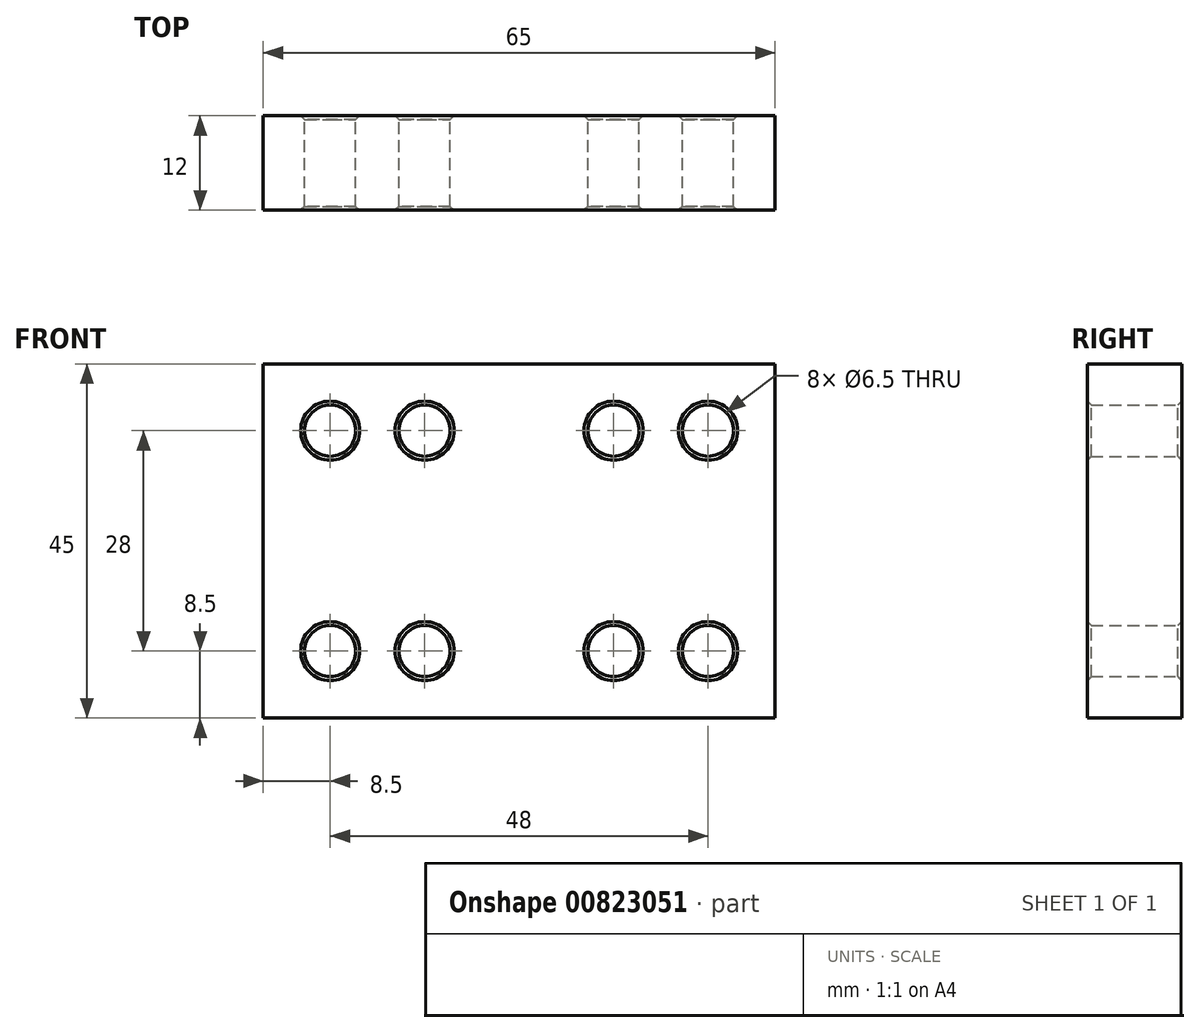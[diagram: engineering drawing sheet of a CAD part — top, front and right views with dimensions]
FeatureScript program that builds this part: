
annotation { "Feature Type Name" : "Feature", "Feature Type Description" : "" }
export const myFeature = defineFeature(function(context is Context, id is Id, definition is map)
    precondition{}
    {
        {
            var Q0;
            Q0=qCreatedBy(makeId("Front.planeOp"),FACE);
            var sketch = newSketch(context, id + "F0", { "sketchPlane" : qUnion([Q0])});
            skLineSegment(sketch, "E0.bottom", {"start": v(-24, 14) * mm, "end": v(-12, 14) * mm, "construction": true});
            skLineSegment(sketch, "E0.top", {"start": v(-24, -14) * mm, "end": v(-12, -14) * mm, "construction": true});
            skLineSegment(sketch, "E0.left", {"start": v(-24, 14) * mm, "end": v(-24, -14) * mm, "construction": true});
            skLineSegment(sketch, "E0.right", {"start": v(-12, 14) * mm, "end": v(-12, -14) * mm, "construction": true});
            skPoint(sketch, "E0.middle", {"position": v(-18, 0) * mm});
            skLineSegment(sketch, "E1", {"start": v(0, 0) * mm, "end": v(-18, 0) * mm, "construction": true});
            skLineSegment(sketch, "E2", {"start": v(0, 0) * mm, "end": v(0, 16.75) * mm, "construction": true});
            skCircle(sketch, "E3", {"center": v(-24, 14) * mm, "radius": 3.25 * mm});
            skCircle(sketch, "E4", {"center": v(-12, 14) * mm, "radius": 3.25 * mm});
            skCircle(sketch, "E5", {"center": v(-12, -14) * mm, "radius": 3.25 * mm});
            skCircle(sketch, "E6", {"center": v(-24, -14) * mm, "radius": 3.25 * mm});
            skCircle(sketch, "E7.MirrorC", {"center": v(24, -14) * mm, "radius": 3.25 * mm});
            skCircle(sketch, "E8.MirrorC", {"center": v(12, -14) * mm, "radius": 3.25 * mm});
            skCircle(sketch, "E9.MirrorC", {"center": v(12, 14) * mm, "radius": 3.25 * mm});
            skCircle(sketch, "E10.MirrorC", {"center": v(24, 14) * mm, "radius": 3.25 * mm});
            skLineSegment(sketch, "E11.bottom", {"start": v(-32.5, -22.5) * mm, "end": v(32.5, -22.5) * mm});
            skLineSegment(sketch, "E11.top", {"start": v(-32.5, 22.5) * mm, "end": v(32.5, 22.5) * mm});
            skLineSegment(sketch, "E11.left", {"start": v(-32.5, -22.5) * mm, "end": v(-32.5, 22.5) * mm});
            skLineSegment(sketch, "E11.right", {"start": v(32.5, -22.5) * mm, "end": v(32.5, 22.5) * mm});
            skPoint(sketch, "E11.middle", {"position": v(0, 0) * mm});
            skCircle(sketch, "E12", {"center": v(24, -14) * mm, "radius": 6.5 * mm, "construction": true});
            skSolve(sketch);
        }
        {
            var Q0;
            Q0 = qSketchRegion(id + "F0", true);
            extrude(context, id + "F1", {"entities" : qUnion([Q0]), "depth" : 12 * mm, "offsetDistance" : 25 * mm});
        }
        {
            var Q0;
            Q0=makeQuery(id+"F1.opExtrude","SWEPT_FACE",FACE,{"disambiguationData":[OSD([sQuery(id+"F0.wireOp",EDGE,"E3")])]});
            var Q1;
            Q1=makeQuery(id+"F1.opExtrude","SWEPT_FACE",FACE,{"disambiguationData":[OSD([sQuery(id+"F0.wireOp",EDGE,"E4")])]});
            var Q2;
            Q2=makeQuery(id+"F1.opExtrude","SWEPT_FACE",FACE,{"disambiguationData":[OSD([sQuery(id+"F0.wireOp",EDGE,"E6")])]});
            var Q3;
            Q3=makeQuery(id+"F1.opExtrude","SWEPT_FACE",FACE,{"disambiguationData":[OSD([sQuery(id+"F0.wireOp",EDGE,"E5")])]});
            var Q4;
            Q4=makeQuery(id+"F1.opExtrude","SWEPT_FACE",FACE,{"disambiguationData":[OSD([sQuery(id+"F0.wireOp",EDGE,"E9.MirrorC")])]});
            var Q5;
            Q5=makeQuery(id+"F1.opExtrude","SWEPT_FACE",FACE,{"disambiguationData":[OSD([sQuery(id+"F0.wireOp",EDGE,"E10.MirrorC")])]});
            var Q6;
            Q6=makeQuery(id+"F1.opExtrude","SWEPT_FACE",FACE,{"disambiguationData":[OSD([sQuery(id+"F0.wireOp",EDGE,"E7.MirrorC")])]});
            var Q7;
            Q7=makeQuery(id+"F1.opExtrude","SWEPT_FACE",FACE,{"disambiguationData":[OSD([sQuery(id+"F0.wireOp",EDGE,"E8.MirrorC")])]});
            chamfer(context, id + "F2", {"entities" : qUnion([Q0, Q1, Q2, Q3, Q4, Q5, Q6, Q7]), "width" : 0.5 * mm, "tangentPropagation" : true});
        }
    });
